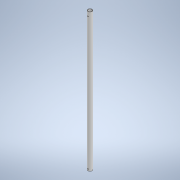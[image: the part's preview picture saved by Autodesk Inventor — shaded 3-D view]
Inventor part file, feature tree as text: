
AUTODESK INVENTOR PART (.ipt)
format: ipt  version: 2022 (Build 260153000, 153)  size: 174,080 bytes
history: native  units: mm
features: extrude x2, sketch x2
ambient origin geometry x8: Origin, YZ Plane, XZ Plane, XY Plane, X Axis, Y Axis, Z Axis, Center Point
bodies: Body1 (feature_tree)
feature tree (4):
  extrude  "Extrusion5"  Depth=15.0mm
  extrude  "Extrusion6"  Depth=10.0mm TaperAngle=0.0deg
  sketch  "Sketch2"  dims[d31=34.456mm d91=15.0mm]
  sketch  "Sketch3"  dims[d92=13.0mm d93=500.0mm d94=0.0mm d95=6.0mm d96=3.0mm d97=20.0mm d98=10.0mm d99=0.0mm d100=0.0mm d101=15.0mm d102=3.0mm]
